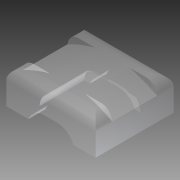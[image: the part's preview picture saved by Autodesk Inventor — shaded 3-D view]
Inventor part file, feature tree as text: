
AUTODESK INVENTOR PART (.ipt)
format: ipt  version: 2012 (Build 160160000, 160)  size: 172,544 bytes
history: native  units: mm
features: mirror x5, extrude x4, fillet x4, sketch x4
ambient origin geometry x8: Origin, YZ Plane, XZ Plane, XY Plane, X Axis, Y Axis, Z Axis, Center Point
bodies: Solid1 (feature_tree)
feature tree (17):
  extrude  "Extrusion1"  Depth=7.0mm
  extrude  "Extrusion2"  Depth=3.5mm
  extrude  "Extrusion3"  Depth=1.5mm
  mirror  "Mirror1"
  mirror  "Mirror2"
  extrude  "Extrusion4"  Depth=2.0mm TaperAngle=0.0deg
  fillet  "Fillet1"  Radius=2.0mm
  fillet  "Fillet2"  Radius=2.0mm
  mirror  "Mirror3"
  fillet  "Fillet3"  Radius=1.0mm
  mirror  "Mirror4"
  mirror  "Mirror5"
  fillet  "Fillet4"  Radius=2.0mm
  sketch  "Sketch1"  dims[d0=8.0mm d1=7.0mm]
  sketch  "Sketch2"  dims[d2=4.0mm d3=3.5mm]
  sketch  "Sketch3"  dims[d4=3.0mm d5=0.0mm d6=1.5mm]
  sketch  "Sketch4"  dims[d7=1.5mm d8=0.0mm d9=2.0mm d10=0.0mm d11=2.0mm d12=2.0mm d13=1.0mm d14=2.0mm d15=0.0mm d16=1.5mm d17=0.5mm d18=1.5mm d19=1.0mm]
